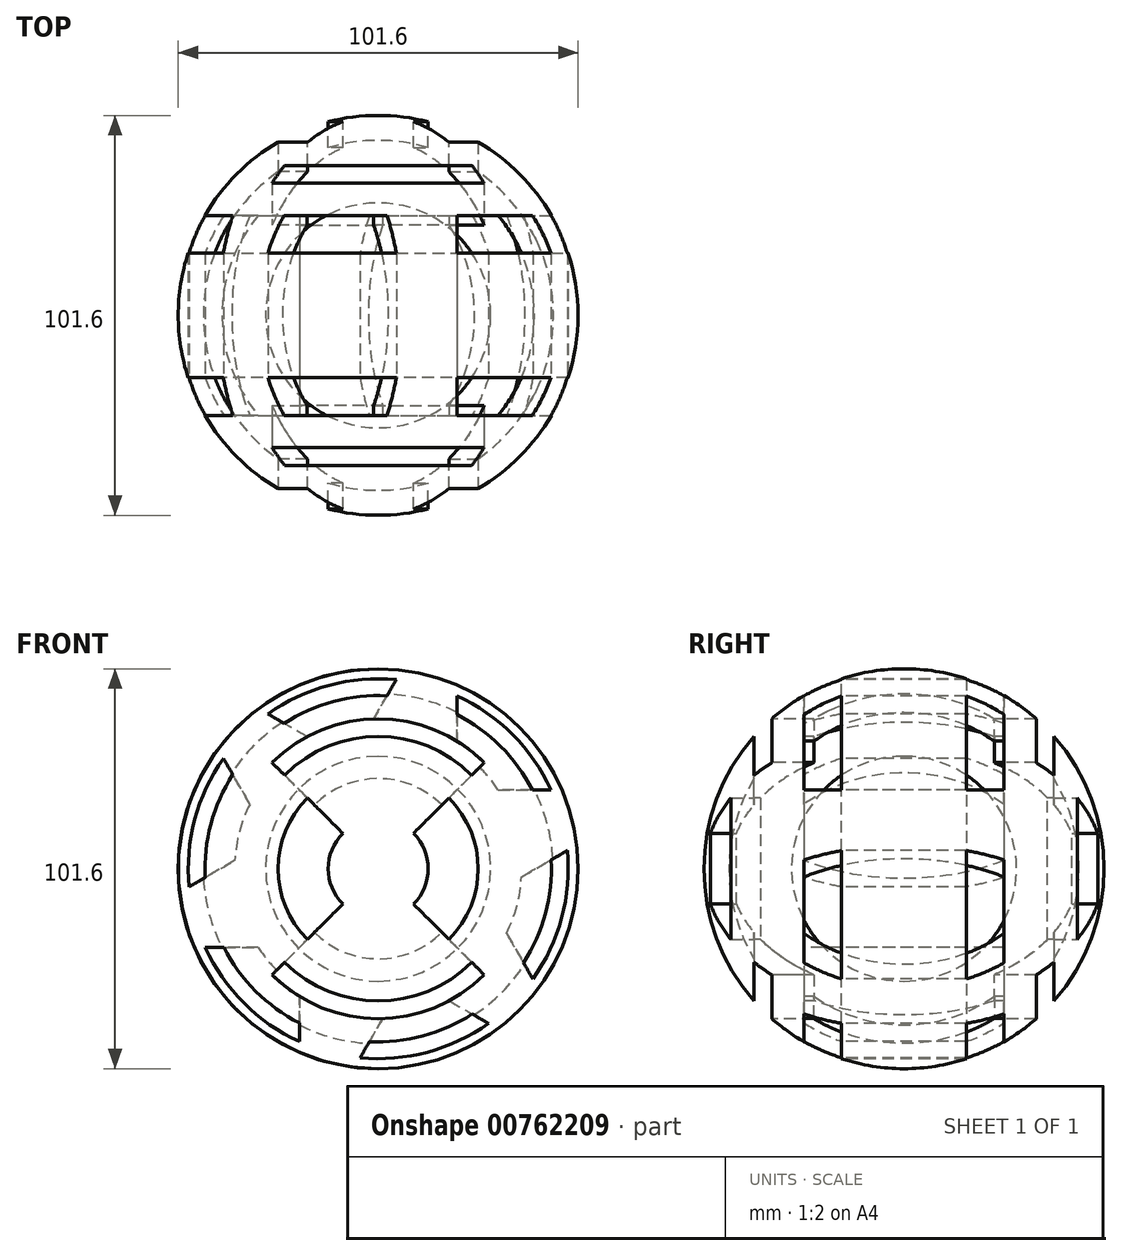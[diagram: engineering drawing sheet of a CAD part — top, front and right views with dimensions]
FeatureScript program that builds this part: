
annotation { "Feature Type Name" : "Feature", "Feature Type Description" : "" }
export const myFeature = defineFeature(function(context is Context, id is Id, definition is map)
    precondition{}
    {
        {
            var Q0;
            Q0=qCreatedBy(makeId("Front.planeOp"),FACE);
            var sketch = newSketch(context, id + "F0", { "sketchPlane" : qUnion([Q0])});
            skArc(sketch, "E0", {"start": v(0, 50.8) * mm, "mid": v(-50.8, 0) * mm, "end": v(0, -50.8) * mm});
            skLineSegment(sketch, "E1", {"start": v(0, 50.8) * mm, "end": v(0, 44.45) * mm});
            skArc(sketch, "E2.0", {"start": v(0, 44.45) * mm, "mid": v(-44.45, 0) * mm, "end": v(0, -44.45) * mm});
            skLineSegment(sketch, "E3.trimOffspring", {"start": v(0, -44.45) * mm, "end": v(0, -50.8) * mm});
            skSolve(sketch);
        }
        {
            var Q0;
            Q0=makeQuery(id+"F0.imprint","IMPRINT",FACE,{"disambiguationData":[TD([[makeQuery(id+"F0.imprint","IMPRINT",EDGE,{"derivedFrom":sQuery(id+"F0.wireOp",EDGE,"E0")}),1.0]])]});
            var Q1;
            Q1=sQuery(id+"F0.wireOp",EDGE,"E1");
            revolve(context, id + "F1", {"surfaceOperationType" : NewSurfaceOperationType.NEW, "entities" : qUnion([Q0]), "axis" : qUnion([Q1]), "revolveType" : RevolveType.FULL});
        }
        {
            var Q0;
            Q0=qCreatedBy(makeId("Front.planeOp"),FACE);
            var sketch = newSketch(context, id + "F2", { "sketchPlane" : qUnion([Q0])});
            skArc(sketch, "E4.0", {"start": v(43.9, 20.03) * mm, "mid": v(34.12, 34.12) * mm, "end": v(20.03, 43.9) * mm});
            skLineSegment(sketch, "E4.1", {"start": v(20.03, 20.03) * mm, "end": v(43.9, 20.03) * mm});
            skLineSegment(sketch, "E4.2", {"start": v(20.03, 20.03) * mm, "end": v(20.03, 43.9) * mm});
            skLineSegment(sketch, "E5.1.0", {"start": v(-7.33, 27.36) * mm, "end": v(-28, 39.3) * mm});
            skLineSegment(sketch, "E5.1.1", {"start": v(-7.33, 27.36) * mm, "end": v(4.6, 48.04) * mm});
            skArc(sketch, "E5.1.2", {"start": v(4.6, 48.04) * mm, "mid": v(-12.5, 46.62) * mm, "end": v(-28, 39.3) * mm});
            skLineSegment(sketch, "E5.2.0", {"start": v(-27.36, 7.33) * mm, "end": v(-48.04, -4.6) * mm});
            skLineSegment(sketch, "E5.2.1", {"start": v(-27.36, 7.33) * mm, "end": v(-39.3, 28) * mm});
            skArc(sketch, "E5.2.2", {"start": v(-39.3, 28) * mm, "mid": v(-46.62, 12.5) * mm, "end": v(-48.04, -4.6) * mm});
            skLineSegment(sketch, "E5.3.0", {"start": v(-20.03, -20.03) * mm, "end": v(-20.03, -43.9) * mm});
            skLineSegment(sketch, "E5.3.1", {"start": v(-20.03, -20.03) * mm, "end": v(-43.9, -20.03) * mm});
            skArc(sketch, "E5.3.2", {"start": v(-43.9, -20.03) * mm, "mid": v(-34.12, -34.12) * mm, "end": v(-20.03, -43.9) * mm});
            skLineSegment(sketch, "E5.4.0", {"start": v(7.33, -27.36) * mm, "end": v(28, -39.3) * mm});
            skLineSegment(sketch, "E5.4.1", {"start": v(7.33, -27.36) * mm, "end": v(-4.6, -48.04) * mm});
            skArc(sketch, "E5.4.2", {"start": v(-4.6, -48.04) * mm, "mid": v(12.5, -46.62) * mm, "end": v(28, -39.3) * mm});
            skLineSegment(sketch, "E5.5.0", {"start": v(27.36, -7.33) * mm, "end": v(48.04, 4.6) * mm});
            skLineSegment(sketch, "E5.5.1", {"start": v(27.36, -7.33) * mm, "end": v(39.3, -28) * mm});
            skArc(sketch, "E5.5.2", {"start": v(39.3, -28) * mm, "mid": v(46.62, -12.5) * mm, "end": v(48.04, 4.6) * mm});
            skSolve(sketch);
        }
        {
            var Q0;
            Q0 = qSketchRegion(id + "F2", true);
            extrude(context, id + "F3", {"entities" : qUnion([Q0]), "operationType" : NewBodyOperationType.REMOVE, "endBound" : BoundingType.SYMMETRIC, "oppositeDirection" : true, "depth" : 50.8 * mm, "offsetDistance" : 25.4 * mm});
        }
        {
            var Q0;
            Q0=qCreatedBy(makeId("Front.planeOp"),FACE);
            var sketch = newSketch(context, id + "F4", { "sketchPlane" : qUnion([Q0])});
            skPoint(sketch, "E6.end.orphan", {"position": v(-11.39, 42.5) * mm});
            skLineSegment(sketch, "E7", {"start": v(0, 0) * mm, "end": v(-26.94, 26.94) * mm});
            skLineSegment(sketch, "E8.1.0", {"start": v(0, 0) * mm, "end": v(-26.94, -26.94) * mm});
            skLineSegment(sketch, "E8.2.0", {"start": v(0, 0) * mm, "end": v(26.94, -26.94) * mm});
            skLineSegment(sketch, "E8.3.0", {"start": v(0, 0) * mm, "end": v(26.94, 26.94) * mm});
            skPoint(sketch, "E8.center", {"position": v(0, 0) * mm});
            skCircle(sketch, "E9", {"center": v(0, 0) * mm, "radius": 25.4 * mm});
            skArc(sketch, "E10", {"start": v(-26.94, -26.94) * mm, "mid": v(0, -38.1) * mm, "end": v(26.94, -26.94) * mm});
            skCircle(sketch, "E11", {"center": v(0, 0) * mm, "radius": 12.7 * mm});
            skPoint(sketch, "E12.orphan", {"position": v(-31.1, 31.1) * mm});
            skPoint(sketch, "E13.orphan", {"position": v(31.1, 31.1) * mm});
            skPoint(sketch, "E14.orphan", {"position": v(31.1, -31.1) * mm});
            skPoint(sketch, "E15.orphan", {"position": v(-31.1, -31.1) * mm});
            skPoint(sketch, "E16.orphan", {"position": v(-23.9, 36.93) * mm});
            skPoint(sketch, "E17.0.end.orphan", {"position": v(2.24, 43.94) * mm});
            skArc(sketch, "E18.trimOffspring", {"start": v(26.94, 26.94) * mm, "mid": v(0, 38.1) * mm, "end": v(-26.94, 26.94) * mm});
            skSolve(sketch);
        }
        {
            var Q0;
            Q0 = qSketchRegion(id + "F4", true);
            extrude(context, id + "F5", {"entities" : qUnion([Q0]), "operationType" : NewBodyOperationType.REMOVE, "endBound" : BoundingType.SYMMETRIC, "oppositeDirection" : true, "depth" : 76.2 * mm, "offsetDistance" : 25.4 * mm});
        }
        {
            var Q0;
            {var subQ0=sQuery(id+"F4.wireOp",EDGE,"E9");var subQ1=sQuery(id+"F4.wireOp",EDGE,"E7");var subQ2=makeQuery(id+"F4.imprint","INTERSECT",VERTEX,{"derivedFrom":[subQ1,subQ0]});Q0=makeQuery(id+"F4.imprint","IMPRINT",FACE,{"disambiguationData":[TD([[makeQuery(id+"F4.imprint","IMPRINT",EDGE,{"disambiguationData":[TD([[subQ2,1.0]])],"derivedFrom":subQ1}),1.0]])]});}
            var Q1;
            {var subQ0=sQuery(id+"F4.wireOp",EDGE,"E9");var subQ1=sQuery(id+"F4.wireOp",EDGE,"E8.2.0");var subQ2=makeQuery(id+"F4.imprint","INTERSECT",VERTEX,{"derivedFrom":[subQ1,subQ0]});Q1=makeQuery(id+"F4.imprint","IMPRINT",FACE,{"disambiguationData":[TD([[makeQuery(id+"F4.imprint","IMPRINT",EDGE,{"disambiguationData":[TD([[subQ2,1.0]])],"derivedFrom":subQ1}),1.0]])]});}
            extrude(context, id + "F6", {"entities" : qUnion([Q0, Q1]), "operationType" : NewBodyOperationType.REMOVE, "endBound" : BoundingType.SYMMETRIC, "depth" : 101.6 * mm, "offsetDistance" : 25.4 * mm});
        }
        {
            var Q0;
            Q0=qCreatedBy(makeId("Front.planeOp"),FACE);
            var sketch = newSketch(context, id + "F7", { "sketchPlane" : qUnion([Q0])});
            skArc(sketch, "E19", {"start": v(0, 28.58) * mm, "mid": v(-28.58, 0) * mm, "end": v(0, -28.58) * mm});
            skLineSegment(sketch, "E20", {"start": v(0, 28.58) * mm, "end": v(0, -28.58) * mm});
            skSolve(sketch);
        }
        {
            var Q0;
            Q0 = qSketchRegion(id + "F7", true);
            var Q1;
            Q1=sQuery(id+"F7.wireOp",EDGE,"E20");
            revolve(context, id + "F8", {"surfaceOperationType" : NewSurfaceOperationType.NEW, "entities" : qUnion([Q0]), "axis" : qUnion([Q1]), "revolveType" : RevolveType.FULL});
        }
    });
